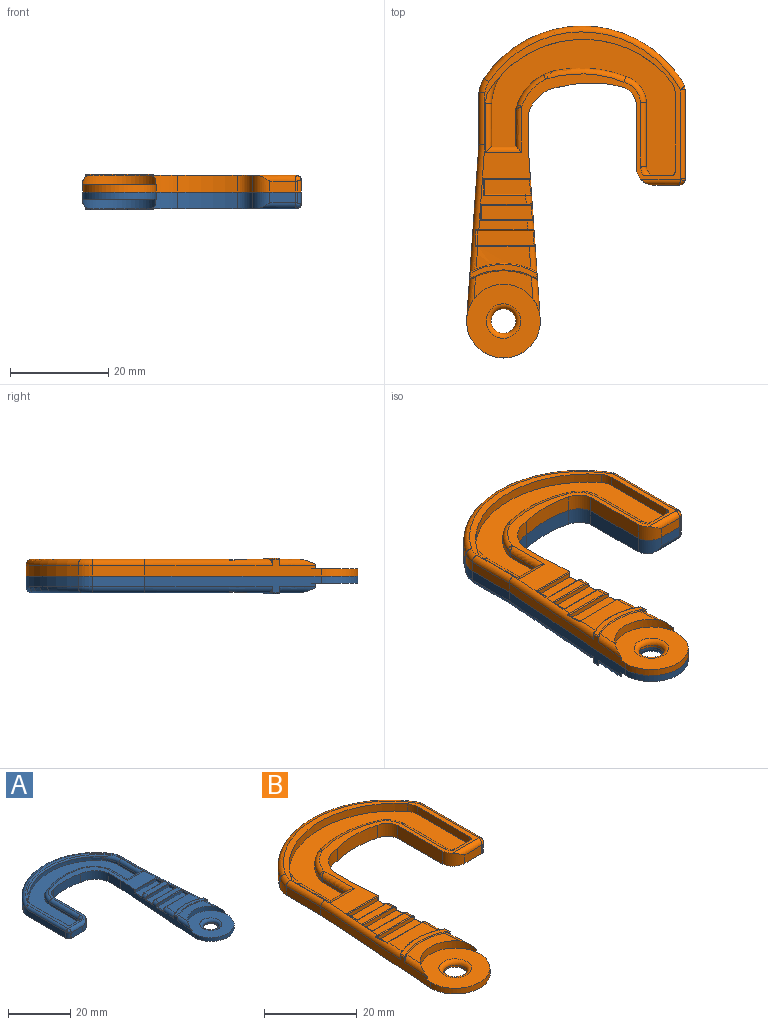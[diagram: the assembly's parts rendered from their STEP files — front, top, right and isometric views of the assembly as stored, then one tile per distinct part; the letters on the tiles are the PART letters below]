
ASSEMBLY  parts=2 mates=1
PART A: 117 faces, bbox 46.8x69.8x4.1 mm
  f0: cylinder r=13.99mm len=1.25mm, axis (0,0,-1), area 0.8mm2, adj f3,f9,f114
  f1: cylinder r=13.99mm len=1.25mm, axis (0,0,-1), area 0.8mm2, adj f5,f9,f115
  f2: cylinder r=13.78mm len=1.25mm, axis (0,0,-1), area 0.8mm2, adj f5,f10,f70
  f3: cylinder r=96265.58mm len=35.88mm, axis (0,0,-1), area 80.3mm2, adj f0,f4,f7,f8,f14,f65,f110,f111
  f4: cylinder r=13.78mm len=1.25mm, axis (0,0,-1), area 0.8mm2, adj f3,f10,f65
  f5: cylinder r=96265.58mm len=35.88mm, axis (0,0,-1), area 86.5mm2, adj f1,f2,f7,f11,f26,f27,f63,f64
  f6: plane 13.38x2.81mm, normal (0,0,1), area 14.7mm2, adj f8,f9,f10,f11
  f7: plane 67.5x44.5mm, normal (0,0,-1), area 1207mm2, adj f3,f5,f14,f15,f16,f17,f18,f19
  f8: torus R=96265.78mm, axis (0,0,1), area 0.4mm2, adj f3,f6,f9,f10
  f9: torus R=14.19mm, axis (0,0,1), area 4.5mm2, adj f0,f1,f6,f8,f11,f113
  f10: torus R=13.58mm, axis (0,0,1), area 4.4mm2, adj f2,f4,f6,f8,f11,f13
  f11: torus R=96265.78mm, axis (0,0,1), area 0.4mm2, adj f5,f6,f9,f10
  f12: plane 10.01x3.98mm, normal (0,0,1), area 18.1mm2, adj f64,f65,f82,f93,f94
  f13: plane 11.12x4.66mm, normal (0,0,1), area 41.6mm2, adj f10,f65,f70,f81
  f14: plane 10.58x2.2mm, normal (1,0,0), area 23.3mm2, adj f3,f7,f15,f66
  f15: cylinder r=6.83mm len=2.89mm, axis (0,0,-1), area 6.8mm2, adj f7,f14,f16,f68
  f16: cylinder r=24.04mm len=40.08mm, axis (0,0,-1), area 104.3mm2, adj f7,f15,f17,f67
  f17: cylinder r=5.37mm len=2.78mm, axis (0,0,-1), area 7.2mm2, adj f7,f16,f18,f67,f76,f77
  f18: plane 17.47x2.4mm, normal (-1,0,0), area 41.9mm2, adj f7,f17,f19,f77
  f19: cylinder r=1.38mm len=2.4mm, axis (0,0,-1), area 3.8mm2, adj f7,f18,f78,f79,f80
  f20: plane 5.17x2.2mm, normal (0,-1,0), area 11.4mm2, adj f7,f21,f69,f80
  f21: cylinder r=3.67mm len=3.6mm, axis (0,0,-1), area 15.7mm2, adj f7,f20,f22,f27,f69
  f22: plane 13.72x3.4mm, normal (1,0,0), area 46.7mm2, adj f7,f21,f23,f27
  f23: cylinder r=4.06mm len=3.4mm, axis (0,0,-1), area 15.8mm2, adj f7,f22,f24,f27
  f24: cylinder r=24.18mm len=12.2mm, axis (0,0,-1), area 41.9mm2, adj f7,f23,f25,f27
  f25: cylinder r=7.39mm len=6.78mm, axis (0,0,-1), area 32.9mm2, adj f7,f24,f26,f27
  f26: plane 5.85x3.4mm, normal (-1,0,0), area 19.9mm2, adj f5,f7,f25,f27
  f27: plane 40.64x35mm, normal (0,0,1), area 202.3mm2, adj f5,f21,f22,f23,f24,f25,f26,f40
  f28: plane 9.44x1mm, normal (0,1,0), area 9.2mm2, adj f29,f31,f89,f90,f91,f92
  f29: plane 3.03x1mm, normal (-1,0,0), area 3mm2, adj f28,f30,f31,f87
  f30: plane 9.2x1mm, normal (0,-1,0), area 9.2mm2, adj f29,f31,f86,f88
  f31: plane 9.43x3.03mm, normal (0,0,1), area 28.2mm2, adj f28,f29,f30,f88,f90
  f32: plane 10.4x1mm, normal (0,1,0), area 10.2mm2, adj f33,f35,f94,f96,f105,f106
  f33: plane 3.03x1mm, normal (-1,0,0), area 3mm2, adj f32,f34,f35,f93
  f34: plane 10.17x1mm, normal (0,-1,0), area 10mm2, adj f33,f35,f98,f99
  f35: plane 10.39x3.03mm, normal (0,0,1), area 31.1mm2, adj f32,f33,f34,f96,f99
  f36: plane 11.89x1.31mm, normal (0,1,0), area 11.4mm2, adj f37,f39,f81,f83,f85,f95,f103,f104
  f37: plane 3.03x0.95mm, normal (-1,0,0), area 2.7mm2, adj f36,f38,f39,f85
  f38: plane 11.36x1mm, normal (0,-1,0), area 11.1mm2, adj f37,f39,f82,f84,f85,f102
  f39: plane 11.57x3.03mm, normal (0,0,1), area 34.7mm2, adj f36,f37,f38,f95,f102
  f40: cylinder r=0.94mm len=2mm, axis (0,0,1), area 2.6mm2, adj f27,f41,f53,f54
  f41: plane 5.88x2.18mm, normal (0,1,0), area 8.2mm2, adj f27,f40,f42,f54,f62
  f42: cylinder r=2.1mm len=1.82mm, axis (0,0,1), area 1.9mm2, adj f41,f43,f54,f62
  f43: plane 13.06x0.8mm, normal (-1,0,0), area 10.4mm2, adj f42,f44,f54,f61
  f44: cylinder r=5.93mm len=5.32mm, axis (0,0,1), area 5.8mm2, adj f43,f45,f54,f60
  f45: cylinder r=25.04mm len=14.26mm, axis (0,0,1), area 11.6mm2, adj f44,f54,f59,f71
  f46: cylinder r=10.74mm len=8.07mm, axis (0,0,1), area 11.4mm2, adj f54,f71,f72,f73,f74,f75
  f47: plane 7.46x0.8mm, normal (1,0,0), area 6mm2, adj f48,f54,f55,f75
  f48: plane 4.94x0.8mm, normal (0,1,0), area 4mm2, adj f47,f49,f54,f56
  f49: plane 8.73x0.8mm, normal (-1,0,0), area 7mm2, adj f48,f50,f54,f57
  f50: cylinder r=12.15mm len=5.75mm, axis (0,0,1), area 4.9mm2, adj f49,f51,f54,f58
  f51: cylinder r=22.94mm len=35.48mm, axis (0,0,1), area 59.5mm2, adj f50,f52,f54,f58,f107
  f52: cylinder r=3.89mm len=2.16mm, axis (0,0,1), area 3.5mm2, adj f51,f53,f54,f108
  f53: plane 17.99x2.08mm, normal (1,0,0), area 32.3mm2, adj f27,f40,f52,f54,f108
  f54: plane 37.34x27.76mm, normal (0,0,1), area 357.2mm2, adj f40,f41,f42,f43,f44,f45,f46,f47
  f55: cylinder r=1.2mm len=9.31mm, axis (0,1,0), area 15.8mm2, adj f27,f47,f56,f74
  f56: cylinder r=1.2mm len=7.34mm, axis (-1,0,0), area 11.6mm2, adj f27,f48,f55,f57
  f57: cylinder r=1.2mm len=9.97mm, axis (0,-1,0), area 17.6mm2, adj f27,f49,f56,f58
  f58: torus R=13.35mm, axis (0,0,1), area 9.2mm2, adj f27,f50,f51,f57,f107
  f59: torus R=23.84mm, axis (0,0,1), area 29.2mm2, adj f27,f45,f60,f72
  f60: torus R=4.73mm, axis (0,0,1), area 12.6mm2, adj f27,f44,f59,f61
  f61: cylinder r=1.2mm len=13.09mm, axis (0,-1,0), area 24.6mm2, adj f27,f43,f60,f62
  f62: torus R=3.3mm, axis (0,0,1), area 4mm2, adj f27,f41,f42,f61
  f63: torus R=96266.78mm, axis (0,0,1), area 3.4mm2, adj f5,f27,f91,f99
  f64: torus R=96266.78mm, axis (0,0,1), area 3.4mm2, adj f5,f12,f102,f105
  f65: torus R=96266.78mm, axis (0,0,1), area 46.8mm2, adj f3,f4,f12,f13,f27,f66,f83,f84
  f66: cylinder r=1.2mm len=10.62mm, axis (0,-1,0), area 19.9mm2, adj f14,f27,f65,f68
  f67: torus R=22.84mm, axis (0,0,1), area 90.2mm2, adj f16,f17,f27,f68,f76
  f68: torus R=5.63mm, axis (0,0,1), area 5.4mm2, adj f15,f27,f66,f67
  f69: cylinder r=1.2mm len=8.06mm, axis (-1,0,0), area 12.5mm2, adj f20,f21,f27,f79
  f70: torus R=96266.78mm, axis (0,0,1), area 9.2mm2, adj f2,f5,f13,f103
  f71: cylinder r=1mm len=0.8mm, axis (0,0,1), area 0mm2, adj f45,f46,f54,f72
  f72: bspline ~2.8x2.1mm, area 2.1mm2, adj f46,f59,f71,f73
  f73: torus R=9.74mm, axis (0,0,1), area 12.6mm2, adj f27,f46,f72,f74
  f74: bspline ~1.32x1.31mm, area 1mm2, adj f46,f55,f73,f75
  f75: cylinder r=1mm len=0.8mm, axis (0,0,1), area 0.2mm2, adj f46,f47,f54,f74
  f76: bspline ~1.28x1.17mm, area 0.4mm2, adj f17,f67,f77
  f77: cylinder r=1mm len=17.96mm, axis (0,1,0), area 28.1mm2, adj f17,f18,f27,f76,f78
  f78: torus R=0.38mm, axis (0,0,1), area 0.7mm2, adj f19,f27,f77,f79
  f79: bspline ~1.44x1.27mm, area 1.5mm2, adj f19,f69,f78,f80
  f80: cylinder r=1mm len=2.2mm, axis (0,0,-1), area 0.9mm2, adj f7,f19,f20,f79
  f81: cylinder r=0.2mm len=10.48mm, axis (-1,0,0), area 3.3mm2, adj f13,f36,f103
  f82: cylinder r=0.2mm len=10.01mm, axis (1,0,0), area 3.1mm2, adj f12,f38,f84,f102
  f83: bspline ~0.47x0.26mm, area 0mm2, adj f36,f65,f85
  f84: bspline ~1.03x0.42mm, area 0.2mm2, adj f38,f65,f82,f85
  f85: bspline ~3.47x0.31mm, area 1.3mm2, adj f36,f37,f38,f65,f83,f84
  f86: cylinder r=0.2mm len=9.6mm, axis (1,0,0), area 3mm2, adj f27,f30,f87,f88
  f87: cylinder r=0.2mm len=3.43mm, axis (0,-1,0), area 1mm2, adj f27,f29,f86,f89
  f88: cylinder r=0.2mm len=1.4mm, axis (0,0,-1), area 0.4mm2, adj f5,f27,f30,f31,f86,f90
  f89: cylinder r=0.2mm len=8.64mm, axis (-1,0,0), area 2.7mm2, adj f27,f28,f87,f91
  f90: torus R=96265.78mm, axis (0,0,1), area 1mm2, adj f5,f28,f31,f88,f92
  f91: bspline ~1.47x1.41mm, area 0.5mm2, adj f28,f63,f89,f92
  f92: cylinder r=0.2mm len=0.2mm, axis (0,0,-1), area 0mm2, adj f5,f28,f90,f91
  f93: cylinder r=0.2mm len=3.43mm, axis (0,-1,0), area 1mm2, adj f12,f33,f65,f94,f97,f98
  f94: cylinder r=0.2mm len=9.6mm, axis (-1,0,0), area 3mm2, adj f12,f32,f93,f105
  f95: torus R=96265.78mm, axis (0,0,1), area 1mm2, adj f5,f36,f39,f101,f104
  f96: torus R=96265.78mm, axis (0,0,1), area 1mm2, adj f5,f32,f35,f100,f106
  f97: bspline ~0.54x0.22mm, area 0mm2, adj f65,f93,f98
  f98: cylinder r=0.2mm len=9.28mm, axis (1,0,0), area 2.9mm2, adj f27,f34,f93,f97,f99
  f99: bspline ~1.47x1.29mm, area 0.6mm2, adj f34,f35,f63,f98,f100
  f100: cylinder r=0.2mm len=0.21mm, axis (0,0,-1), area 0mm2, adj f5,f96,f99
  f101: cylinder r=0.2mm len=0.21mm, axis (0,0,-1), area 0mm2, adj f5,f95,f102
  f102: bspline ~1.49x1.47mm, area 0.6mm2, adj f38,f39,f64,f82,f101
  f103: bspline ~1.47x1.27mm, area 0.5mm2, adj f36,f70,f81,f104
  f104: cylinder r=0.2mm len=0.2mm, axis (0,0,-1), area 0mm2, adj f5,f36,f95,f103
  f105: bspline ~1.47x1.47mm, area 0.5mm2, adj f32,f64,f94,f106
  f106: cylinder r=0.2mm len=0.2mm, axis (0,0,-1), area 0mm2, adj f5,f32,f96,f105
  f107: torus R=23.44mm, axis (0,0,1), area 32.9mm2, adj f27,f51,f58,f108
  f108: torus R=4.39mm, axis (0,0,1), area 1.2mm2, adj f27,f52,f53,f107
  f109: cylinder r=2.5mm len=5mm, axis (0,0,-1), area 7.9mm2, adj f7,f116
  f110: cylinder r=7.5mm len=15mm, axis (0,0,-1), area 35.3mm2, adj f3,f5,f7,f111
  f111: plane 15x15mm, normal (0,0,1), area 138.2mm2, adj f3,f5,f110,f112,f116
  f112: cylinder r=7.5mm len=14.85mm, axis (0,0,-1), area 36.2mm2, adj f3,f5,f111,f113,f114,f115
  f113: plane 11.96x5.68mm, normal (0,0,1), area 36.5mm2, adj f9,f112,f114,f115
  f114: torus R=96266.78mm, axis (0,0,1), area 11.2mm2, adj f0,f3,f112,f113
  f115: torus R=96266.78mm, axis (0,0,1), area 11.2mm2, adj f1,f5,f112,f113
  f116: torus R=3.5mm, axis (0,0,1), area 28.3mm2, adj f109,f111
PART B: 115 faces, bbox 46.8x69.8x4.1 mm
  f0: cylinder r=96265.58mm len=35.88mm, axis (0,0,-1), area 80.3mm2, adj f3,f4,f5,f6,f8,f12,f13,f16
  f1: cylinder r=96265.58mm len=35.88mm, axis (0,0,-1), area 86.5mm2, adj f3,f4,f5,f6,f9,f11,f14,f19
  f2: cylinder r=2.5mm len=5mm, axis (0,0,-1), area 7.9mm2, adj f5,f10
  f3: cylinder r=7.5mm len=15mm, axis (0,0,-1), area 35.3mm2, adj f0,f1,f4,f5
  f4: plane 15x15mm, normal (0,0,1), area 138.2mm2, adj f0,f1,f3,f6,f10
  f5: plane 67.5x44.5mm, normal (0,0,-1), area 1207mm2, adj f0,f1,f2,f3,f22,f23,f24,f25
  f6: cylinder r=7.5mm len=14.85mm, axis (0,0,-1), area 36.2mm2, adj f0,f1,f4,f7,f8,f9
  f7: plane 11.96x5.68mm, normal (0,0,1), area 36.5mm2, adj f6,f8,f9,f17
  f8: torus R=96266.78mm, axis (0,0,1), area 11.2mm2, adj f0,f6,f7,f12
  f9: torus R=96266.78mm, axis (0,0,1), area 11.2mm2, adj f1,f6,f7,f11
  f10: torus R=3.5mm, axis (0,0,1), area 28.3mm2, adj f2,f4
  f11: cylinder r=13.99mm len=1.25mm, axis (0,0,-1), area 0.8mm2, adj f1,f9,f17
  f12: cylinder r=13.99mm len=1.25mm, axis (0,0,-1), area 0.8mm2, adj f0,f8,f17
  f13: cylinder r=13.78mm len=1.25mm, axis (0,0,-1), area 0.8mm2, adj f0,f18,f73
  f14: cylinder r=13.78mm len=1.25mm, axis (0,0,-1), area 0.8mm2, adj f1,f18,f78
  f15: plane 13.38x2.81mm, normal (0,0,1), area 14.7mm2, adj f16,f17,f18,f19
  f16: torus R=96265.78mm, axis (0,0,1), area 0.4mm2, adj f0,f15,f17,f18
  f17: torus R=14.19mm, axis (0,0,1), area 4.5mm2, adj f7,f11,f12,f15,f16,f19
  f18: torus R=13.58mm, axis (0,0,1), area 4.4mm2, adj f13,f14,f15,f16,f19,f21
  f19: torus R=96265.78mm, axis (0,0,1), area 0.4mm2, adj f1,f15,f17,f18
  f20: plane 10.01x3.98mm, normal (0,0,1), area 18.1mm2, adj f72,f73,f90,f101,f102
  f21: plane 11.12x4.66mm, normal (0,0,1), area 41.6mm2, adj f18,f73,f78,f89
  f22: plane 10.58x2.2mm, normal (-1,0,0), area 23.3mm2, adj f0,f5,f23,f74
  f23: cylinder r=6.83mm len=2.89mm, axis (0,0,-1), area 6.8mm2, adj f5,f22,f24,f76
  f24: cylinder r=24.04mm len=40.08mm, axis (0,0,-1), area 104.3mm2, adj f5,f23,f25,f75
  f25: cylinder r=5.37mm len=2.78mm, axis (0,0,-1), area 7.2mm2, adj f5,f24,f26,f75,f84,f85
  f26: plane 17.47x2.4mm, normal (1,0,0), area 41.9mm2, adj f5,f25,f27,f85
  f27: cylinder r=1.38mm len=2.4mm, axis (0,0,-1), area 3.8mm2, adj f5,f26,f86,f87,f88
  f28: plane 5.17x2.2mm, normal (0,-1,0), area 11.4mm2, adj f5,f29,f77,f88
  f29: cylinder r=3.67mm len=3.6mm, axis (0,0,-1), area 15.7mm2, adj f5,f28,f30,f35,f77
  f30: plane 13.72x3.4mm, normal (-1,0,0), area 46.7mm2, adj f5,f29,f31,f35
  f31: cylinder r=4.06mm len=3.4mm, axis (0,0,-1), area 15.8mm2, adj f5,f30,f32,f35
  f32: cylinder r=24.18mm len=12.2mm, axis (0,0,-1), area 41.9mm2, adj f5,f31,f33,f35
  f33: cylinder r=7.39mm len=6.78mm, axis (0,0,-1), area 32.9mm2, adj f5,f32,f34,f35
  f34: plane 5.85x3.4mm, normal (1,0,0), area 19.9mm2, adj f1,f5,f33,f35
  f35: plane 40.64x35mm, normal (0,0,1), area 224.8mm2, adj f1,f29,f30,f31,f32,f33,f34,f48
  f36: plane 9.44x1mm, normal (0,1,0), area 9.2mm2, adj f37,f39,f97,f98,f99,f100
  f37: plane 3.03x1mm, normal (1,0,0), area 3mm2, adj f36,f38,f39,f95
  f38: plane 9.2x1mm, normal (0,-1,0), area 9.2mm2, adj f37,f39,f94,f96
  f39: plane 9.43x3.03mm, normal (0,0,1), area 28.2mm2, adj f36,f37,f38,f96,f98
  f40: plane 10.4x1mm, normal (0,1,0), area 10.2mm2, adj f41,f43,f102,f104,f113,f114
  f41: plane 3.03x1mm, normal (1,0,0), area 3mm2, adj f40,f42,f43,f101
  f42: plane 10.17x1mm, normal (0,-1,0), area 10mm2, adj f41,f43,f106,f107
  f43: plane 10.39x3.03mm, normal (0,0,1), area 31.1mm2, adj f40,f41,f42,f104,f107
  f44: plane 11.89x1.31mm, normal (0,1,0), area 11.4mm2, adj f45,f47,f89,f91,f93,f103,f111,f112
  f45: plane 3.03x0.95mm, normal (1,0,0), area 2.7mm2, adj f44,f46,f47,f93
  f46: plane 11.36x1mm, normal (0,-1,0), area 11.1mm2, adj f45,f47,f90,f92,f93,f110
  f47: plane 11.57x3.03mm, normal (0,0,1), area 34.7mm2, adj f44,f45,f46,f103,f110
  f48: cylinder r=0.94mm len=2mm, axis (0,0,1), area 2.6mm2, adj f35,f49,f61,f62
  f49: plane 5.88x2.18mm, normal (0,1,0), area 8.2mm2, adj f35,f48,f50,f62,f70
  f50: cylinder r=2.1mm len=1.82mm, axis (0,0,1), area 1.9mm2, adj f49,f51,f62,f70
  f51: plane 13.06x0.8mm, normal (1,0,0), area 10.4mm2, adj f50,f52,f62,f69
  f52: cylinder r=5.93mm len=5.32mm, axis (0,0,1), area 5.8mm2, adj f51,f53,f62,f68
  f53: cylinder r=25.04mm len=14.26mm, axis (0,0,1), area 11.6mm2, adj f52,f62,f67,f79
  f54: cylinder r=10.74mm len=8.07mm, axis (0,0,1), area 11.4mm2, adj f62,f79,f80,f81,f82,f83
  f55: plane 7.46x0.8mm, normal (-1,0,0), area 6mm2, adj f56,f62,f63,f83
  f56: plane 4.94x0.8mm, normal (0,1,0), area 4mm2, adj f55,f57,f62,f64
  f57: plane 8.73x0.8mm, normal (1,0,0), area 7mm2, adj f56,f58,f62,f65
  f58: cylinder r=12.15mm len=5.75mm, axis (0,0,1), area 4.9mm2, adj f57,f59,f62,f66
  f59: cylinder r=22.94mm len=37.55mm, axis (0,0,1), area 80.3mm2, adj f35,f58,f60,f62,f66
  f60: cylinder r=3.89mm len=2.16mm, axis (0,0,1), area 4.6mm2, adj f35,f59,f61,f62
  f61: plane 15.96x2mm, normal (-1,0,0), area 31.9mm2, adj f35,f48,f60,f62
  f62: plane 37.34x27.76mm, normal (0,0,1), area 357.2mm2, adj f48,f49,f50,f51,f52,f53,f54,f55
  f63: cylinder r=1.2mm len=9.31mm, axis (0,1,0), area 15.8mm2, adj f35,f55,f64,f82
  f64: cylinder r=1.2mm len=7.34mm, axis (1,0,0), area 11.6mm2, adj f35,f56,f63,f65
  f65: cylinder r=1.2mm len=9.97mm, axis (0,-1,0), area 17.6mm2, adj f35,f57,f64,f66
  f66: torus R=13.35mm, axis (0,0,1), area 7.7mm2, adj f35,f58,f59,f65
  f67: torus R=23.84mm, axis (0,0,1), area 29.2mm2, adj f35,f53,f68,f80
  f68: torus R=4.73mm, axis (0,0,1), area 12.6mm2, adj f35,f52,f67,f69
  f69: cylinder r=1.2mm len=13.09mm, axis (0,-1,0), area 24.6mm2, adj f35,f51,f68,f70
  f70: torus R=3.3mm, axis (0,0,1), area 4mm2, adj f35,f49,f50,f69
  f71: torus R=96266.78mm, axis (0,0,1), area 3.4mm2, adj f1,f35,f99,f107
  f72: torus R=96266.78mm, axis (0,0,1), area 3.4mm2, adj f1,f20,f110,f113
  f73: torus R=96266.78mm, axis (0,0,1), area 46.7mm2, adj f0,f13,f20,f21,f35,f74,f91,f92
  f74: cylinder r=1.2mm len=10.62mm, axis (0,-1,0), area 19.9mm2, adj f22,f35,f73,f76
  f75: torus R=22.84mm, axis (0,0,1), area 90.2mm2, adj f24,f25,f35,f76,f84
  f76: torus R=5.63mm, axis (0,0,1), area 5.4mm2, adj f23,f35,f74,f75
  f77: cylinder r=1.2mm len=8.06mm, axis (1,0,0), area 12.5mm2, adj f28,f29,f35,f87
  f78: torus R=96266.78mm, axis (0,0,1), area 9.2mm2, adj f1,f14,f21,f111
  f79: cylinder r=1mm len=0.8mm, axis (0,0,1), area 0mm2, adj f53,f54,f62,f80
  f80: bspline ~2.8x2.1mm, area 2.1mm2, adj f54,f67,f79,f81
  f81: torus R=9.74mm, axis (0,0,1), area 12.6mm2, adj f35,f54,f80,f82
  f82: bspline ~1.32x1.31mm, area 1mm2, adj f54,f63,f81,f83
  f83: cylinder r=1mm len=0.8mm, axis (0,0,1), area 0.2mm2, adj f54,f55,f62,f82
  f84: bspline ~1.28x1.17mm, area 0.4mm2, adj f25,f75,f85
  f85: cylinder r=1mm len=17.96mm, axis (0,1,0), area 28.1mm2, adj f25,f26,f35,f84,f86
  f86: torus R=0.38mm, axis (0,0,1), area 0.7mm2, adj f27,f35,f85,f87
  f87: bspline ~1.44x1.27mm, area 1.5mm2, adj f27,f77,f86,f88
  f88: cylinder r=1mm len=2.2mm, axis (0,0,-1), area 0.9mm2, adj f5,f27,f28,f87
  f89: cylinder r=0.2mm len=10.48mm, axis (1,0,0), area 3.3mm2, adj f21,f44,f111
  f90: cylinder r=0.2mm len=10.01mm, axis (-1,0,0), area 3.1mm2, adj f20,f46,f92,f110
  f91: bspline ~0.47x0.26mm, area 0mm2, adj f44,f73,f93
  f92: bspline ~1.03x0.42mm, area 0.2mm2, adj f46,f73,f90,f93
  f93: bspline ~5.02x0.41mm, area 1.3mm2, adj f44,f45,f46,f73,f91,f92
  f94: cylinder r=0.2mm len=9.6mm, axis (-1,0,0), area 3mm2, adj f35,f38,f95,f96
  f95: cylinder r=0.2mm len=3.43mm, axis (0,-1,0), area 1mm2, adj f35,f37,f94,f97
  f96: cylinder r=0.2mm len=1.4mm, axis (0,0,-1), area 0.4mm2, adj f1,f35,f38,f39,f94,f98
  f97: cylinder r=0.2mm len=8.64mm, axis (1,0,0), area 2.7mm2, adj f35,f36,f95,f99
  f98: torus R=96265.78mm, axis (0,0,1), area 1mm2, adj f1,f36,f39,f96,f100
  f99: bspline ~1.47x1.41mm, area 0.5mm2, adj f36,f71,f97,f100
  f100: cylinder r=0.2mm len=0.2mm, axis (0,0,-1), area 0mm2, adj f1,f36,f98,f99
  f101: cylinder r=0.2mm len=3.43mm, axis (0,-1,0), area 1mm2, adj f20,f41,f73,f102,f105,f106
  f102: cylinder r=0.2mm len=9.6mm, axis (1,0,0), area 3mm2, adj f20,f40,f101,f113
  f103: torus R=96265.78mm, axis (0,0,1), area 1mm2, adj f1,f44,f47,f109,f112
  f104: torus R=96265.78mm, axis (0,0,1), area 1mm2, adj f1,f40,f43,f108,f114
  f105: bspline ~0.54x0.22mm, area 0mm2, adj f73,f101,f106
  f106: cylinder r=0.2mm len=9.28mm, axis (-1,0,0), area 2.9mm2, adj f35,f42,f101,f105,f107
  f107: bspline ~1.49x1.47mm, area 0.6mm2, adj f42,f43,f71,f106,f108
  f108: cylinder r=0.2mm len=0.21mm, axis (0,0,-1), area 0mm2, adj f1,f104,f107
  f109: cylinder r=0.2mm len=0.21mm, axis (0,0,-1), area 0mm2, adj f1,f103,f110
  f110: bspline ~1.47x1.29mm, area 0.6mm2, adj f46,f47,f72,f90,f109
  f111: bspline ~1.47x1.47mm, area 0.5mm2, adj f44,f78,f89,f112
  f112: cylinder r=0.2mm len=0.2mm, axis (0,0,-1), area 0mm2, adj f1,f44,f103,f111
  f113: bspline ~1.47x1.27mm, area 0.5mm2, adj f40,f72,f102,f114
  f114: cylinder r=0.2mm len=0.2mm, axis (0,0,-1), area 0mm2, adj f1,f40,f104,f113
PLACE A rot(axis=(0,1,0),180deg) t=(75.98,0,-1.5)mm
PLACE B t=(0,0,-1.5)mm
MATE fastened B.f2 <-> A.f109  axis (0,0,-1) through (67.99,-35.54,-1.5)mm
